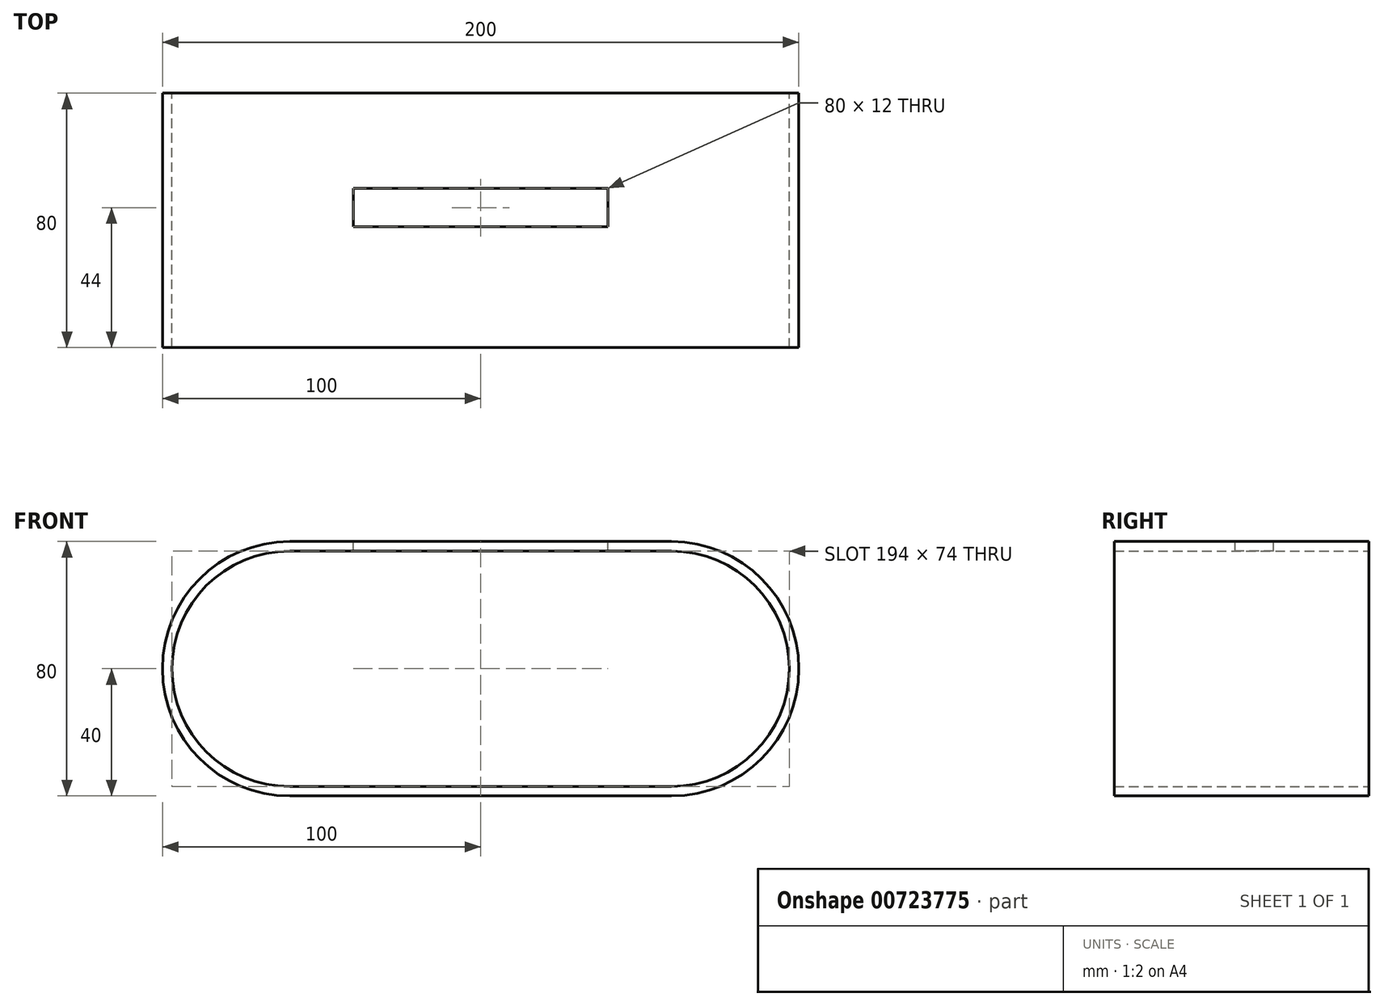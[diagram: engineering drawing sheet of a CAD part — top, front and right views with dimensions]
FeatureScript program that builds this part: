
annotation { "Feature Type Name" : "Feature", "Feature Type Description" : "" }
export const myFeature = defineFeature(function(context is Context, id is Id, definition is map)
    precondition{}
    {
        {
            var Q0;
            Q0=qCreatedBy(makeId("Front.planeOp"),FACE);
            var sketch = newSketch(context, id + "F0", { "sketchPlane" : qUnion([Q0])});
            skLineSegment(sketch, "E0.bottom", {"start": v(-60, 40) * mm, "end": v(60, 40) * mm});
            skLineSegment(sketch, "E0.top", {"start": v(-60, -40) * mm, "end": v(60, -40) * mm});
            skLineSegment(sketch, "E0.left", {"start": v(-100, 0) * mm, "end": v(-100, 0) * mm});
            skLineSegment(sketch, "E0.right", {"start": v(100, 0) * mm, "end": v(100, 0) * mm});
            skPoint(sketch, "E0.middle", {"position": v(0, 0) * mm});
            skPoint(sketch, "E1.visualSharp", {"position": v(-100, 40) * mm});
            skArc(sketch, "E1.filletArc", {"start": v(-60, 40) * mm, "mid": v(-88.28, 28.28) * mm, "end": v(-100, 0) * mm});
            skPoint(sketch, "E2.visualSharp", {"position": v(-100, -40) * mm});
            skArc(sketch, "E2.filletArc", {"start": v(-100, 0) * mm, "mid": v(-88.28, -28.28) * mm, "end": v(-60, -40) * mm});
            skPoint(sketch, "E3.visualSharp", {"position": v(100, -40) * mm});
            skArc(sketch, "E3.filletArc", {"start": v(60, -40) * mm, "mid": v(88.28, -28.28) * mm, "end": v(100, 0) * mm});
            skPoint(sketch, "E4.visualSharp", {"position": v(100, 40) * mm});
            skArc(sketch, "E4.filletArc", {"start": v(100, 0) * mm, "mid": v(88.28, 28.28) * mm, "end": v(60, 40) * mm});
            skArc(sketch, "E5.0", {"start": v(-60, 37) * mm, "mid": v(-86.16, 26.16) * mm, "end": v(-97, 0) * mm});
            skLineSegment(sketch, "E6.0", {"start": v(-60, 37) * mm, "end": v(60, 37) * mm});
            skArc(sketch, "E6.1", {"start": v(-97, 0) * mm, "mid": v(-86.16, -26.16) * mm, "end": v(-60, -37) * mm});
            skLineSegment(sketch, "E6.2", {"start": v(-60, -37) * mm, "end": v(60, -37) * mm});
            skArc(sketch, "E6.3", {"start": v(60, -37) * mm, "mid": v(86.16, -26.16) * mm, "end": v(97, 0) * mm});
            skArc(sketch, "E6.4", {"start": v(97, 0) * mm, "mid": v(86.16, 26.16) * mm, "end": v(60, 37) * mm});
            skSolve(sketch);
        }
        {
            var Q0;
            Q0=makeQuery(id+"F0.imprint","IMPRINT",FACE,{"disambiguationData":[TD([[makeQuery(id+"F0.imprint","IMPRINT",EDGE,{"derivedFrom":sQuery(id+"F0.wireOp",EDGE,"E0.bottom")}),-1.0]])]});
            extrude(context, id + "F1", {"entities" : qUnion([Q0]), "depth" : 80 * mm});
        }
        {
            var Q0;
            Q0=makeQuery(id+"F1.opExtrude","SWEPT_FACE",FACE,{"disambiguationData":[OSD([sQuery(id+"F0.wireOp",EDGE,"E0.bottom")])]});
            var sketch = newSketch(context, id + "F2", { "sketchPlane" : qUnion([Q0])});
            skLineSegment(sketch, "E7.bottom", {"start": v(-40, -30) * mm, "end": v(40, -30) * mm});
            skLineSegment(sketch, "E7.top", {"start": v(-40, -42) * mm, "end": v(40, -42) * mm});
            skLineSegment(sketch, "E7.left", {"start": v(-40, -30) * mm, "end": v(-40, -42) * mm});
            skLineSegment(sketch, "E7.right", {"start": v(40, -30) * mm, "end": v(40, -42) * mm});
            skSolve(sketch);
        }
        {
            var Q0;
            Q0=makeQuery(id+"F2.imprint","IMPRINT",FACE,{"disambiguationData":[TD([[makeQuery(id+"F2.imprint","IMPRINT",EDGE,{"derivedFrom":sQuery(id+"F2.wireOp",EDGE,"E7.bottom")}),-1.0]])]});
            extrude(context, id + "F3", {"entities" : qUnion([Q0]), "operationType" : NewBodyOperationType.REMOVE, "oppositeDirection" : true, "depth" : 25 * mm, "offsetDistance" : 25 * mm});
        }
    });
